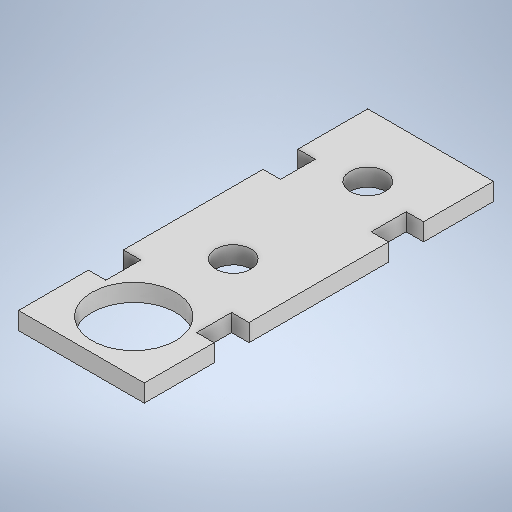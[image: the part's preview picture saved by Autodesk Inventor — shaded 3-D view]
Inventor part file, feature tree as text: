
AUTODESK INVENTOR PART (.ipt)
format: ipt  version: 2025.2 (Build 292293000, 293)  size: 265,728 bytes
history: native  units: mm
features: extrude x1, sketch x1
ambient origin geometry x8: Origin, YZ Plane, XZ Plane, XY Plane, X Axis, Y Axis, Z Axis, Center Point
bodies: Solid1 (feature_tree)
feature tree (2):
  extrude  "Extrusion1"  Depth=100.0mm
  sketch  "Sketch2"  dims[d0=36.0mm d1=100.0mm d2=20.0mm d3=20.0mm d4=10.0mm d5=5.0mm d6=10.0mm d7=5.0mm d8=5.0mm d9=15.0mm d10=24.0mm d15=5.0mm d16=0.0mm d17=28.5mm d18=10.1mm d19=38.5mm d20=10.1mm]
